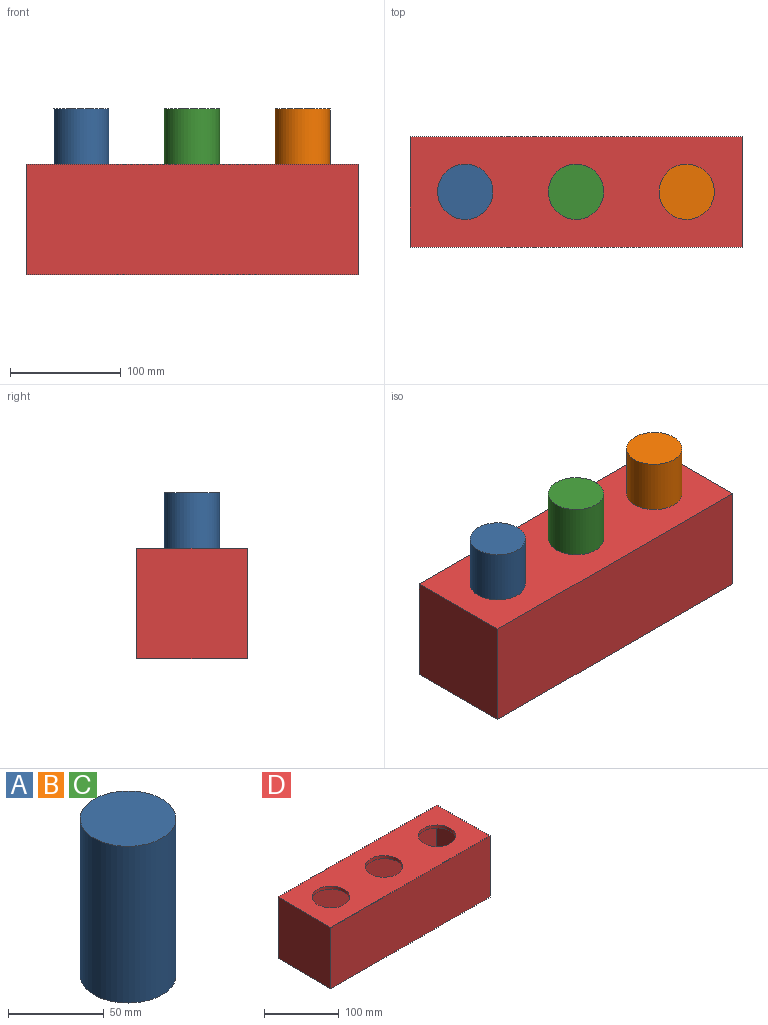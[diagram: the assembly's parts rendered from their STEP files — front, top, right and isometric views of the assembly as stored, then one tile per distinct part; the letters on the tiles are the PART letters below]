
ASSEMBLY  parts=4 mates=3
PART A: 3 faces, bbox 50x50x100 mm
  f0: cylinder r=25mm len=100mm, axis (0,0,-1), area 15708mm2, adj f1,f2
  f1: plane 50x50mm, normal (0,0,1), area 1963.5mm2, adj f0
  f2: plane 50x50mm, normal (0,0,-1), area 1963.5mm2, adj f0
PART B: same geometry as A
PART C: same geometry as A
PART D: 15 faces, bbox 300x100x100 mm
  f0: plane 300x100mm, normal (0,0,1), area 24109.5mm2, adj f1,f2,f3,f4,f6,f7,f8
  f1: plane 100x100mm, normal (1,0,0), area 10000mm2, adj f0,f2,f4,f5
  f2: plane 300x100mm, normal (0,1,0), area 30000mm2, adj f0,f1,f3,f5
  f3: plane 100x100mm, normal (-1,0,0), area 10000mm2, adj f0,f2,f4,f5
  f4: plane 300x100mm, normal (0,-1,0), area 30000mm2, adj f0,f1,f3,f5
  f5: plane 300x100mm, normal (0,0,-1), area 30000mm2, adj f1,f2,f3,f4
  f6: cylinder r=25mm len=50mm, axis (0,0,1), area 785.4mm2, adj f0,f9
  f7: cylinder r=25mm len=50mm, axis (0,0,1), area 785.4mm2, adj f0,f9
  f8: cylinder r=25mm len=50mm, axis (0,0,1), area 785.4mm2, adj f0,f9
  f9: plane 290x90mm, normal (0,0,-1), area 20209.5mm2, adj f6,f7,f8,f10,f11,f12,f13
  f10: plane 90x90mm, normal (-1,0,0), area 8100mm2, adj f9,f11,f13,f14
  f11: plane 290x90mm, normal (0,-1,0), area 26100mm2, adj f9,f10,f12,f14
  f12: plane 90x90mm, normal (1,0,0), area 8100mm2, adj f9,f11,f13,f14
  f13: plane 290x90mm, normal (0,1,0), area 26100mm2, adj f9,f10,f12,f14
  f14: plane 290x90mm, normal (0,0,1), area 26100mm2, adj f10,f11,f12,f13
PLACE A t=(-100,0,0)mm
PLACE B t=(100,0,0)mm
PLACE C at identity
PLACE D at identity fixed
MATE slider D.f8 <-> A.f0  axis (0,0,1) through (-100,0,100)mm
MATE slider D.f7 <-> B.f0  axis (0,0,1) through (100,0,100)mm
MATE slider C.f0 <-> D.f6  axis (0,0,-1) through (0,0,100)mm
